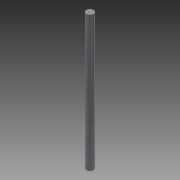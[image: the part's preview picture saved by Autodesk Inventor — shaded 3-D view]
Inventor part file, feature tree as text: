
AUTODESK INVENTOR PART (.ipt)
format: ipt  version: 2015 SP1 (Build 190203100, 203)  size: 66,048 bytes
history: native  units: mm
features: extrude x1, sketch x1
ambient origin geometry x8: Origin, YZ Plane, XZ Plane, XY Plane, X Axis, Y Axis, Z Axis, Center Point
bodies: Solid1 (feature_tree)
feature tree (2):
  extrude  "Extrusion1"  Depth=152.4mm TaperAngle=0.0deg
  sketch  "Sketch1"  dims[d0=8.0mm d1=152.4mm d2=0.0mm]
